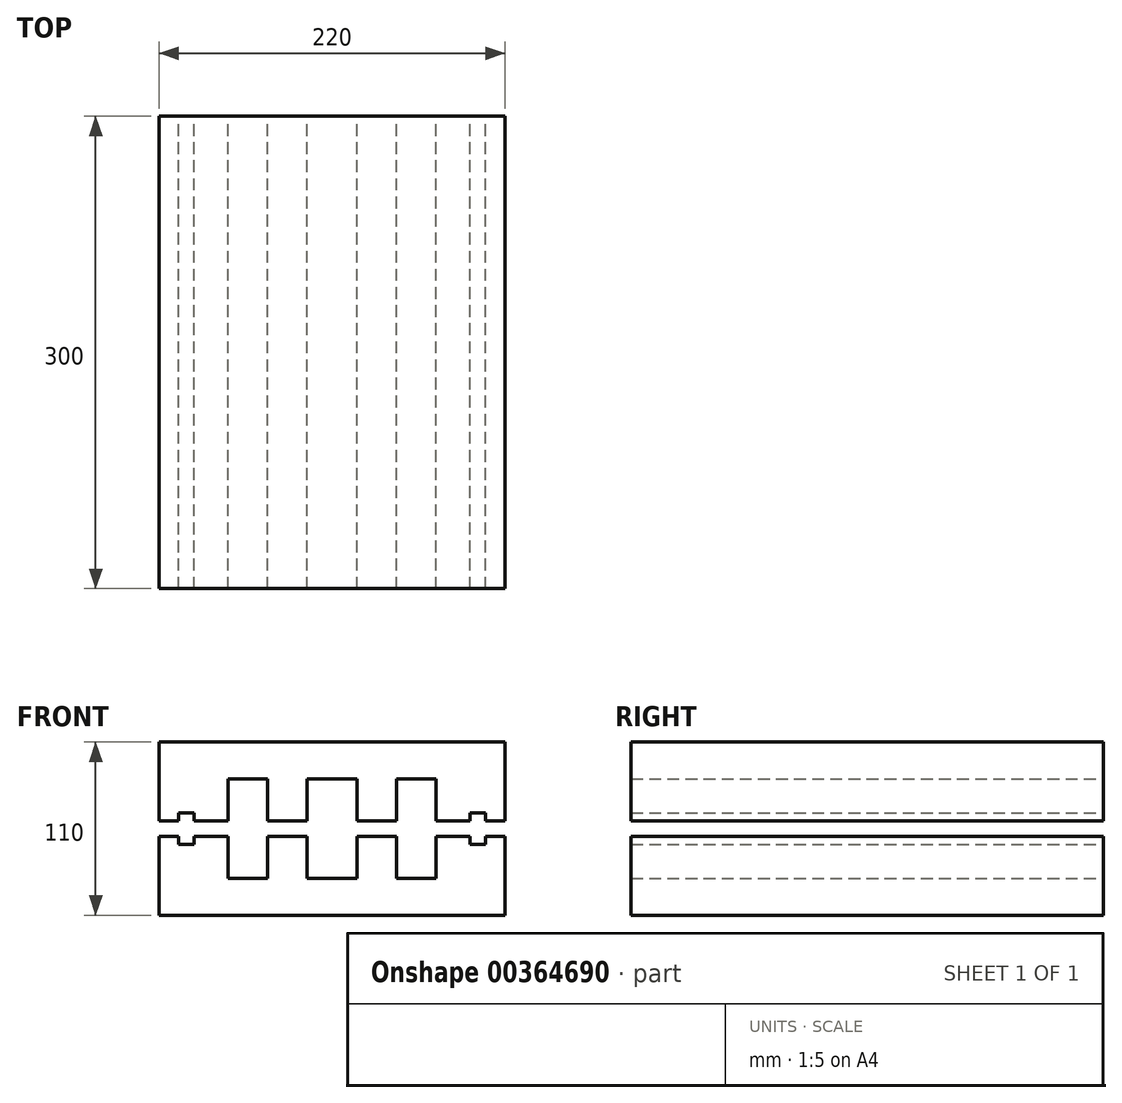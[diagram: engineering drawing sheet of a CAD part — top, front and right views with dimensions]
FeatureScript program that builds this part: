
annotation { "Feature Type Name" : "Feature", "Feature Type Description" : "" }
export const myFeature = defineFeature(function(context is Context, id is Id, definition is map)
    precondition{}
    {
        {
            var Q0;
            Q0=qCreatedBy(makeId("Front.planeOp"),FACE);
            var sketch = newSketch(context, id + "F0", { "sketchPlane" : qUnion([Q0])});
            skLineSegment(sketch, "E0", {"start": v(0, 0) * mm, "end": v(-110, 0) * mm});
            skLineSegment(sketch, "E1", {"start": v(0, 0) * mm, "end": v(110, 0) * mm});
            skLineSegment(sketch, "E2.0", {"start": v(0, 40) * mm, "end": v(-110, 40) * mm});
            skLineSegment(sketch, "E2.1", {"start": v(0, 40) * mm, "end": v(110, 40) * mm});
            skLineSegment(sketch, "E3.0", {"start": v(0, -40) * mm, "end": v(110, -40) * mm});
            skLineSegment(sketch, "E3.1", {"start": v(0, -40) * mm, "end": v(-110, -40) * mm});
            skLineSegment(sketch, "E4.0", {"start": v(0, -55) * mm, "end": v(-110, -55) * mm});
            skLineSegment(sketch, "E4.1", {"start": v(0, -55) * mm, "end": v(110, -55) * mm});
            skLineSegment(sketch, "E5.0", {"start": v(0, 55) * mm, "end": v(110, 55) * mm});
            skLineSegment(sketch, "E5.1", {"start": v(0, 55) * mm, "end": v(-110, 55) * mm});
            skLineSegment(sketch, "E6", {"start": v(-110, 55) * mm, "end": v(-110, 40) * mm});
            skLineSegment(sketch, "E7", {"start": v(-110, -40) * mm, "end": v(-110, -55) * mm});
            skLineSegment(sketch, "E8", {"start": v(110, 55) * mm, "end": v(110, 40) * mm});
            skLineSegment(sketch, "E9", {"start": v(110, -40) * mm, "end": v(110, -55) * mm});
            skLineSegment(sketch, "E10", {"start": v(-110, 40) * mm, "end": v(-110, 0) * mm});
            skLineSegment(sketch, "E11", {"start": v(-110, -40) * mm, "end": v(-110, 0) * mm});
            skLineSegment(sketch, "E12", {"start": v(110, 40) * mm, "end": v(110, 0) * mm});
            skLineSegment(sketch, "E13", {"start": v(110, -40) * mm, "end": v(110, 0) * mm});
            skLineSegment(sketch, "E14.bottom", {"start": v(-16, -31.5) * mm, "end": v(16, -31.5) * mm});
            skLineSegment(sketch, "E14.top", {"start": v(-16, 31.5) * mm, "end": v(16, 31.5) * mm});
            skLineSegment(sketch, "E14.left", {"start": v(-16, -31.5) * mm, "end": v(-16, 31.5) * mm});
            skLineSegment(sketch, "E14.right", {"start": v(16, -31.5) * mm, "end": v(16, 31.5) * mm});
            skPoint(sketch, "E14.middle", {"position": v(0, 0) * mm});
            skLineSegment(sketch, "E15.bottom", {"start": v(-110, -5) * mm, "end": v(110, -5) * mm});
            skLineSegment(sketch, "E15.top", {"start": v(-110, 5) * mm, "end": v(110, 5) * mm});
            skLineSegment(sketch, "E15.left", {"start": v(-110, -5) * mm, "end": v(-110, 5) * mm});
            skLineSegment(sketch, "E15.right", {"start": v(110, -5) * mm, "end": v(110, 5) * mm});
            skLineSegment(sketch, "E16.top", {"start": v(-16, -5) * mm, "end": v(-41, -5) * mm});
            skLineSegment(sketch, "E16.left", {"start": v(-16, -31.5) * mm, "end": v(-16, -5) * mm});
            skLineSegment(sketch, "E16.right", {"start": v(-41, -31.5) * mm, "end": v(-41, -5) * mm});
            skLineSegment(sketch, "E17.bottom", {"start": v(-41, -31.5) * mm, "end": v(-66, -31.5) * mm});
            skLineSegment(sketch, "E17.top", {"start": v(-41, -5) * mm, "end": v(-66, -5) * mm});
            skLineSegment(sketch, "E17.right", {"start": v(-66, -31.5) * mm, "end": v(-66, -5) * mm});
            skLineSegment(sketch, "E18.top", {"start": v(-66, -5) * mm, "end": v(-91, -5) * mm});
            skLineSegment(sketch, "E19.top", {"start": v(16, -5) * mm, "end": v(41, -5) * mm});
            skLineSegment(sketch, "E19.left", {"start": v(16, -31.5) * mm, "end": v(16, -5) * mm});
            skLineSegment(sketch, "E19.right", {"start": v(41, -31.5) * mm, "end": v(41, -5) * mm});
            skLineSegment(sketch, "E20.bottom", {"start": v(41, -5) * mm, "end": v(66, -5) * mm});
            skLineSegment(sketch, "E20.top", {"start": v(41, -31.5) * mm, "end": v(66, -31.5) * mm});
            skLineSegment(sketch, "E20.left", {"start": v(41, -5) * mm, "end": v(41, -31.5) * mm});
            skLineSegment(sketch, "E20.right", {"start": v(66, -5) * mm, "end": v(66, -31.5) * mm});
            skLineSegment(sketch, "E21.bottom", {"start": v(-66, 5) * mm, "end": v(-41, 5) * mm});
            skLineSegment(sketch, "E21.top", {"start": v(-66, 31.5) * mm, "end": v(-41, 31.5) * mm});
            skLineSegment(sketch, "E21.left", {"start": v(-66, 5) * mm, "end": v(-66, 31.5) * mm});
            skLineSegment(sketch, "E21.right", {"start": v(-41, 5) * mm, "end": v(-41, 31.5) * mm});
            skLineSegment(sketch, "E22.bottom", {"start": v(41, 5) * mm, "end": v(66, 5) * mm});
            skLineSegment(sketch, "E22.top", {"start": v(41, 31.5) * mm, "end": v(66, 31.5) * mm});
            skLineSegment(sketch, "E22.left", {"start": v(41, 5) * mm, "end": v(41, 31.5) * mm});
            skLineSegment(sketch, "E22.right", {"start": v(66, 5) * mm, "end": v(66, 31.5) * mm});
            skLineSegment(sketch, "E23.bottom", {"start": v(-110, 5) * mm, "end": v(-75, 5) * mm});
            skLineSegment(sketch, "E23.left", {"start": v(-110, 5) * mm, "end": v(-110, 31.5) * mm});
            skLineSegment(sketch, "E24.bottom", {"start": v(-97.5, -10) * mm, "end": v(-87.5, -10) * mm});
            skLineSegment(sketch, "E24.top", {"start": v(-97.5, 10) * mm, "end": v(-87.5, 10) * mm});
            skLineSegment(sketch, "E24.left", {"start": v(-97.5, -10) * mm, "end": v(-97.5, 10) * mm});
            skLineSegment(sketch, "E24.right", {"start": v(-87.5, -10) * mm, "end": v(-87.5, 10) * mm});
            skPoint(sketch, "E24.middle", {"position": v(-92.5, 0) * mm});
            skPoint(sketch, "E24.middle.positionSnap0", {"position": v(-92.5, 5) * mm});
            skPoint(sketch, "E24.centerSnap0", {"position": v(-92.5, 5) * mm});
            skLineSegment(sketch, "E25.bottom", {"start": v(110, 5) * mm, "end": v(75, 5) * mm});
            skLineSegment(sketch, "E25.left", {"start": v(110, 5) * mm, "end": v(110, 31.5) * mm});
            skLineSegment(sketch, "E26.bottom", {"start": v(87.5, 10) * mm, "end": v(97.5, 10) * mm});
            skLineSegment(sketch, "E26.top", {"start": v(87.5, -10) * mm, "end": v(97.5, -10) * mm});
            skLineSegment(sketch, "E26.left", {"start": v(87.5, 10) * mm, "end": v(87.5, -10) * mm});
            skLineSegment(sketch, "E26.right", {"start": v(97.5, 10) * mm, "end": v(97.5, -10) * mm});
            skPoint(sketch, "E26.middle", {"position": v(92.5, 0) * mm});
            skPoint(sketch, "E26.middle.positionSnap0", {"position": v(92.5, 5) * mm});
            skPoint(sketch, "E26.centerSnap0", {"position": v(92.5, 5) * mm});
            skSolve(sketch);
        }
        {
            var Q0;
            Q0=makeQuery(id+"F0.imprint","IMPRINT",FACE,{"disambiguationData":[TD([[makeQuery(id+"F0.imprint","IMPRINT",EDGE,{"derivedFrom":sQuery(id+"F0.wireOp",EDGE,"E2.0")}),-1.0]])]});
            var Q1;
            Q1=makeQuery(id+"F0.imprint","IMPRINT",FACE,{"disambiguationData":[TD([[makeQuery(id+"F0.imprint","IMPRINT",EDGE,{"derivedFrom":sQuery(id+"F0.wireOp",EDGE,"E3.0")}),-1.0]])]});
            var Q2;
            Q2=makeQuery(id+"F0.imprint","IMPRINT",FACE,{"disambiguationData":[TD([[makeQuery(id+"F0.imprint","IMPRINT",EDGE,{"derivedFrom":sQuery(id+"F0.wireOp",EDGE,"E3.0")}),1.0]])]});
            var Q3;
            Q3=makeQuery(id+"F0.imprint","IMPRINT",FACE,{"disambiguationData":[TD([[makeQuery(id+"F0.imprint","IMPRINT",EDGE,{"derivedFrom":sQuery(id+"F0.wireOp",EDGE,"E2.0")}),1.0]])]});
            extrude(context, id + "F1", {"entities" : qUnion([Q0, Q1, Q2, Q3]), "depth" : 300 * mm});
        }
    });
